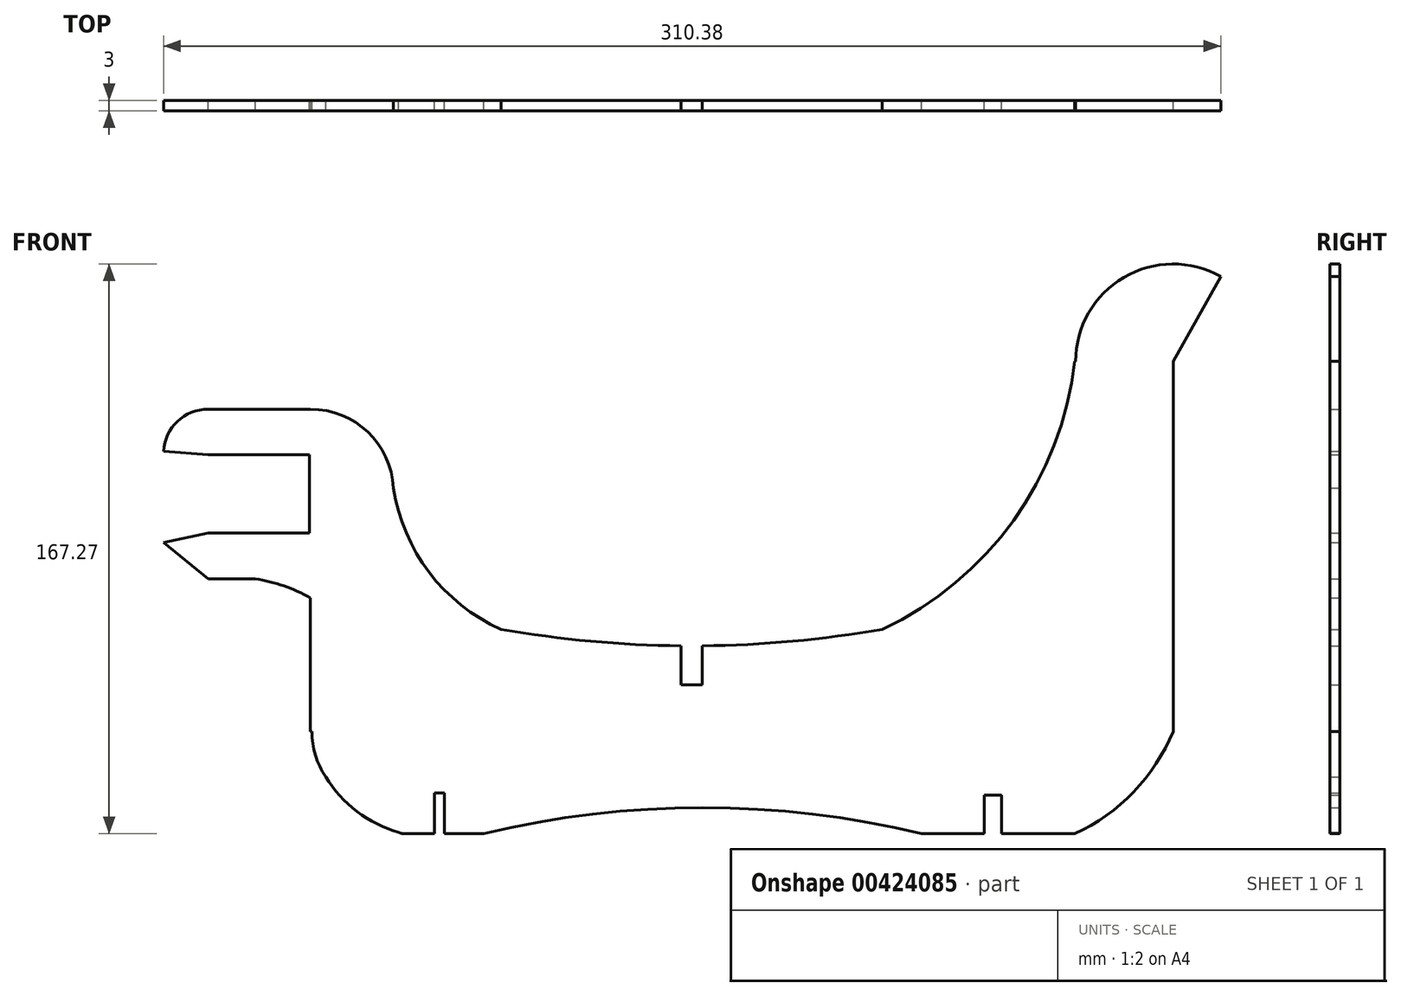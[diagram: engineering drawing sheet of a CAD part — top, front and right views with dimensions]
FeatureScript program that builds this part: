
annotation { "Feature Type Name" : "Feature", "Feature Type Description" : "" }
export const myFeature = defineFeature(function(context is Context, id is Id, definition is map)
    precondition{}
    {
        {
            var Q0;
            Q0=qCreatedBy(makeId("Front.planeOp"),FACE);
            var sketch = newSketch(context, id + "F0", { "sketchPlane" : qUnion([Q0])});
            skLineSegment(sketch, "E0.bottom", {"start": v(-100, 30) * mm, "end": v(-68.45, 30) * mm});
            skLineSegment(sketch, "E0.top", {"start": v(-97, -30) * mm, "end": v(-87.95, -30) * mm});
            skLineSegment(sketch, "E0.left", {"start": v(-100, 30) * mm, "end": v(-100, -27) * mm});
            skLineSegment(sketch, "E0.right", {"start": v(100, 30) * mm, "end": v(100, -30) * mm});
            skPoint(sketch, "E0.middle", {"position": v(0, 0) * mm});
            skPoint(sketch, "E1", {"position": v(-86.5, -30) * mm});
            skPoint(sketch, "E2", {"position": v(75.98, -30) * mm});
            skLineSegment(sketch, "E3.top", {"start": v(-87.95, -18.07) * mm, "end": v(-85.05, -18.07) * mm});
            skLineSegment(sketch, "E3.left", {"start": v(-87.95, -30) * mm, "end": v(-87.95, -18.07) * mm});
            skLineSegment(sketch, "E3.right", {"start": v(-85.05, -30) * mm, "end": v(-85.05, -18.07) * mm});
            skPoint(sketch, "E4.visualSharp", {"position": v(-100, -30) * mm});
            skArc(sketch, "E4.filletArc", {"start": v(-100, -27) * mm, "mid": v(-99.12, -29.12) * mm, "end": v(-97, -30) * mm});
            skArc(sketch, "E5", {"start": v(55.03, -30) * mm, "mid": v(-9.24, -22.36) * mm, "end": v(-73.5, -30) * mm});
            skLineSegment(sketch, "E6.trimOffspring", {"start": v(55.03, -30) * mm, "end": v(73.46, -30) * mm});
            skLineSegment(sketch, "E7.bottom", {"start": v(-100, 0) * mm, "end": v(-124.38, 0) * mm});
            skLineSegment(sketch, "E7.top", {"start": v(-100, 71.5) * mm, "end": v(-124.38, 71.5) * mm});
            skLineSegment(sketch, "E7.left", {"start": v(-100, 0) * mm, "end": v(-100, 71.5) * mm});
            skLineSegment(sketch, "E7.right", {"start": v(-124.38, 0) * mm, "end": v(-124.38, 71.5) * mm});
            skArc(sketch, "E8", {"start": v(-85.05, -18.7) * mm, "mid": v(-113.54, 19.75) * mm, "end": v(-87.95, -20.7) * mm});
            skArc(sketch, "E9", {"start": v(-100, 71.5) * mm, "mid": v(-89.53, 46.72) * mm, "end": v(-68.45, 30) * mm});
            skLineSegment(sketch, "E10.bottom", {"start": v(-124.38, 44.82) * mm, "end": v(-154.41, 44.82) * mm});
            skLineSegment(sketch, "E10.top", {"start": v(-124.38, 94.64) * mm, "end": v(-154.41, 94.64) * mm});
            skLineSegment(sketch, "E10.left", {"start": v(-124.38, 44.82) * mm, "end": v(-124.38, 94.64) * mm});
            skLineSegment(sketch, "E10.right", {"start": v(-154.41, 44.82) * mm, "end": v(-154.41, 58.23) * mm});
            skArc(sketch, "E11", {"start": v(-100, 71.5) * mm, "mid": v(-107.58, 87.93) * mm, "end": v(-124.38, 94.64) * mm});
            skArc(sketch, "E12", {"start": v(-124.38, 39.19) * mm, "mid": v(-132.21, 42.75) * mm, "end": v(-140.56, 44.82) * mm});
            skLineSegment(sketch, "E13.bottom", {"start": v(-124.7, 81.23) * mm, "end": v(-154.41, 81.23) * mm});
            skLineSegment(sketch, "E13.top", {"start": v(-124.7, 58.23) * mm, "end": v(-154.41, 58.23) * mm});
            skLineSegment(sketch, "E13.left", {"start": v(-124.7, 81.23) * mm, "end": v(-124.7, 58.23) * mm});
            skPoint(sketch, "E13.middle", {"position": v(-154.41, 69.73) * mm});
            skPoint(sketch, "E14.orphan", {"position": v(-184.13, 81.23) * mm});
            skPoint(sketch, "E15.orphan", {"position": v(-184.13, 58.23) * mm});
            skLineSegment(sketch, "E16.trimOffspring", {"start": v(-154.41, 81.23) * mm, "end": v(-154.41, 94.64) * mm});
            skLineSegment(sketch, "E17.bottom", {"start": v(73.46, -18.73) * mm, "end": v(78.5, -18.73) * mm});
            skLineSegment(sketch, "E17.left", {"start": v(73.46, -18.73) * mm, "end": v(73.46, -30) * mm});
            skLineSegment(sketch, "E17.right", {"start": v(78.5, -18.73) * mm, "end": v(78.5, -30) * mm});
            skLineSegment(sketch, "E18.bottom", {"start": v(100, 0) * mm, "end": v(128.88, 0) * mm});
            skLineSegment(sketch, "E18.top", {"start": v(100, 108.64) * mm, "end": v(128.88, 108.64) * mm});
            skLineSegment(sketch, "E18.left", {"start": v(100, 0) * mm, "end": v(100, 108.64) * mm});
            skLineSegment(sketch, "E18.right", {"start": v(128.88, 0) * mm, "end": v(128.88, 108.64) * mm});
            skArc(sketch, "E19", {"start": v(100, -30) * mm, "mid": v(117.3, -17.75) * mm, "end": v(128.88, 0) * mm});
            skArc(sketch, "E20", {"start": v(43.5, 30) * mm, "mid": v(82.01, 61.95) * mm, "end": v(100, 108.64) * mm});
            skArc(sketch, "E21", {"start": v(142.86, 133.62) * mm, "mid": v(101.18, 115.87) * mm, "end": v(128.88, 80.02) * mm});
            skArc(sketch, "E22", {"start": v(128.88, 105.95) * mm, "mid": v(114.5, 107.97) * mm, "end": v(100, 108.64) * mm});
            skLineSegment(sketch, "E23", {"start": v(128.88, 108.64) * mm, "end": v(142.86, 133.62) * mm});
            skPoint(sketch, "E24.orphan", {"position": v(73.46, -41.27) * mm});
            skPoint(sketch, "E25.orphan", {"position": v(78.5, -41.27) * mm});
            skLineSegment(sketch, "E26.trimOffspring", {"start": v(78.5, -30) * mm, "end": v(100, -30) * mm});
            skPoint(sketch, "E3.bottom.end.orphan", {"position": v(-85.05, -41.93) * mm});
            skPoint(sketch, "E3.bottom.start.orphan", {"position": v(-87.95, -41.93) * mm});
            skArc(sketch, "E27", {"start": v(-68.45, 30) * mm, "mid": v(-42.13, 26.5) * mm, "end": v(-15.62, 25.16) * mm});
            skLineSegment(sketch, "E28.trimOffspring", {"start": v(43.5, 30) * mm, "end": v(100, 30) * mm});
            skLineSegment(sketch, "E29.bottom", {"start": v(-15.62, 13.64) * mm, "end": v(-9.32, 13.64) * mm});
            skLineSegment(sketch, "E29.left", {"start": v(-15.62, 13.64) * mm, "end": v(-15.62, 25.16) * mm});
            skLineSegment(sketch, "E29.right", {"start": v(-9.32, 13.64) * mm, "end": v(-9.32, 25.16) * mm});
            skPoint(sketch, "E29.middle", {"position": v(-12.47, 25.14) * mm});
            skPoint(sketch, "E29.top.start.orphan", {"position": v(-15.62, 36.65) * mm});
            skPoint(sketch, "E30.orphan", {"position": v(-9.32, 36.65) * mm});
            skArc(sketch, "E31.trimOffspring", {"start": v(-9.32, 25.16) * mm, "mid": v(17.2, 26.5) * mm, "end": v(43.5, 30) * mm});
            skLineSegment(sketch, "E32.trimOffspring", {"start": v(-85.05, -30) * mm, "end": v(-73.5, -30) * mm});
            skArc(sketch, "E33", {"start": v(-122.41, -8.44) * mm, "mid": v(-112.27, -22.24) * mm, "end": v(-97, -30) * mm});
            skArc(sketch, "E34", {"start": v(-154.41, 94.64) * mm, "mid": v(-163.42, 91.06) * mm, "end": v(-167.52, 82.28) * mm});
            skLineSegment(sketch, "E35", {"start": v(-167.52, 82.28) * mm, "end": v(-154.41, 81.23) * mm});
            skLineSegment(sketch, "E36", {"start": v(-154.41, 58.23) * mm, "end": v(-167.52, 55.5) * mm});
            skLineSegment(sketch, "E37", {"start": v(-167.52, 55.5) * mm, "end": v(-154.41, 44.82) * mm});
            skSolve(sketch);
        }
        {
            var Q0;
            Q0 = qSketchRegion(id + "F0", true);
            extrude(context, id + "F1", {"entities" : qUnion([Q0]), "depth" : 3 * mm});
        }
    });
